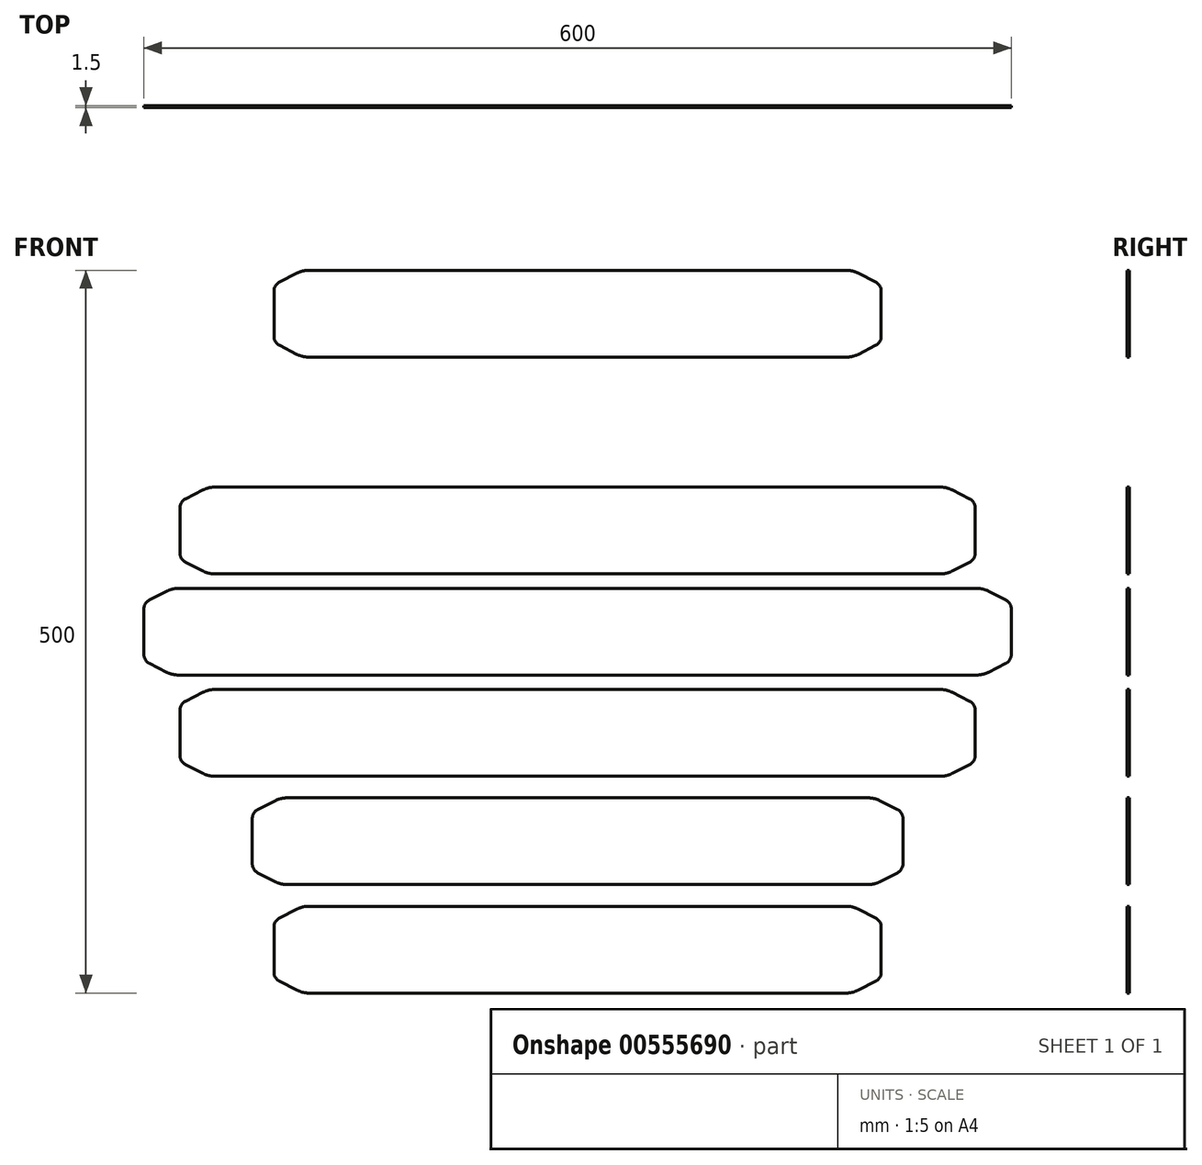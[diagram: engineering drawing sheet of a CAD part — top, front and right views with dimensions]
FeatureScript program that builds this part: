
annotation { "Feature Type Name" : "Feature", "Feature Type Description" : "" }
export const myFeature = defineFeature(function(context is Context, id is Id, definition is map)
    precondition{}
    {
        {
            var Q0;
            Q0=qCreatedBy(makeId("Front.planeOp"),FACE);
            var sketch = newSketch(context, id + "F0", { "sketchPlane" : qUnion([Q0])});
            skLineSegment(sketch, "E0", {"start": v(-284.17, 28.04) * mm, "end": v(-296.18, 21.92) * mm});
            skLineSegment(sketch, "E1", {"start": v(-300, 15.68) * mm, "end": v(-300, 0) * mm});
            skLineSegment(sketch, "E2", {"start": v(-300, 0) * mm, "end": v(0, 0) * mm, "construction": true});
            skLineSegment(sketch, "E3", {"start": v(-276, 30) * mm, "end": v(0, 30) * mm});
            skLineSegment(sketch, "E4", {"start": v(0, 30) * mm, "end": v(0, 0) * mm, "construction": true});
            skPoint(sketch, "E5.visualSharp", {"position": v(-280.32, 30) * mm});
            skArc(sketch, "E5.filletArc", {"start": v(-276, 30) * mm, "mid": v(-280.2, 29.5) * mm, "end": v(-284.17, 28.04) * mm});
            skPoint(sketch, "E6.visualSharp", {"position": v(-300, 19.97) * mm});
            skArc(sketch, "E6.filletArc", {"start": v(-296.18, 21.92) * mm, "mid": v(-298.97, 19.34) * mm, "end": v(-300, 15.68) * mm});
            skLineSegment(sketch, "E7.MirrorCS", {"start": v(-300, -15.68) * mm, "end": v(-300, 0) * mm});
            skArc(sketch, "E8.MirrorCS", {"start": v(-296.18, -21.92) * mm, "mid": v(-298.97, -19.34) * mm, "end": v(-300, -15.68) * mm});
            skLineSegment(sketch, "E9.MirrorCS", {"start": v(-284.17, -28.04) * mm, "end": v(-296.18, -21.92) * mm});
            skLineSegment(sketch, "E10.MirrorCS", {"start": v(-276, -30) * mm, "end": v(0, -30) * mm});
            skArc(sketch, "E11.MirrorCS", {"start": v(-276, -30) * mm, "mid": v(-280.2, -29.5) * mm, "end": v(-284.17, -28.04) * mm});
            skLineSegment(sketch, "E12.MirrorCS", {"start": v(276, 30) * mm, "end": v(0, 30) * mm});
            skLineSegment(sketch, "E13.MirrorCS", {"start": v(276, -30) * mm, "end": v(0, -30) * mm});
            skLineSegment(sketch, "E14.MirrorCS", {"start": v(300, -15.68) * mm, "end": v(300, 0) * mm});
            skLineSegment(sketch, "E15.MirrorCS", {"start": v(300, 15.68) * mm, "end": v(300, 0) * mm});
            skPoint(sketch, "E16.MirrorP", {"position": v(300, 19.97) * mm});
            skArc(sketch, "E17.MirrorCS", {"start": v(296.18, 21.92) * mm, "mid": v(298.97, 19.34) * mm, "end": v(300, 15.68) * mm});
            skLineSegment(sketch, "E18.MirrorCS", {"start": v(284.17, 28.04) * mm, "end": v(296.18, 21.92) * mm});
            skArc(sketch, "E19.MirrorCS", {"start": v(276, 30) * mm, "mid": v(280.2, 29.5) * mm, "end": v(284.17, 28.04) * mm});
            skArc(sketch, "E20.MirrorCS", {"start": v(276, -30) * mm, "mid": v(280.2, -29.5) * mm, "end": v(284.17, -28.04) * mm});
            skLineSegment(sketch, "E21.MirrorCS", {"start": v(284.17, -28.04) * mm, "end": v(296.18, -21.92) * mm});
            skArc(sketch, "E22.MirrorCS", {"start": v(296.18, -21.92) * mm, "mid": v(298.97, -19.34) * mm, "end": v(300, -15.68) * mm});
            skLineSegment(sketch, "E23", {"start": v(-259.17, -41.96) * mm, "end": v(-271.18, -48.08) * mm});
            skLineSegment(sketch, "E24", {"start": v(-275, -54.32) * mm, "end": v(-275, -70) * mm});
            skLineSegment(sketch, "E25", {"start": v(-275, -70) * mm, "end": v(0, -70) * mm, "construction": true});
            skLineSegment(sketch, "E26", {"start": v(-251, -40) * mm, "end": v(0, -40) * mm});
            skLineSegment(sketch, "E27", {"start": v(0, -40) * mm, "end": v(0, -70) * mm, "construction": true});
            skPoint(sketch, "E28.visualSharp", {"position": v(-255.32, -40) * mm});
            skArc(sketch, "E28.filletArc", {"start": v(-251, -40) * mm, "mid": v(-255.2, -40.5) * mm, "end": v(-259.17, -41.96) * mm});
            skPoint(sketch, "E29.visualSharp", {"position": v(-275, -50.03) * mm});
            skArc(sketch, "E29.filletArc", {"start": v(-271.18, -48.08) * mm, "mid": v(-273.97, -50.66) * mm, "end": v(-275, -54.32) * mm});
            skLineSegment(sketch, "E30.MirrorCS", {"start": v(-275, -85.68) * mm, "end": v(-275, -70) * mm});
            skArc(sketch, "E31.MirrorCS", {"start": v(-271.18, -91.92) * mm, "mid": v(-273.97, -89.34) * mm, "end": v(-275, -85.68) * mm});
            skLineSegment(sketch, "E32.MirrorCS", {"start": v(-259.17, -98.04) * mm, "end": v(-271.18, -91.92) * mm});
            skLineSegment(sketch, "E33.MirrorCS", {"start": v(-251, -100) * mm, "end": v(0, -100) * mm});
            skArc(sketch, "E34.MirrorCS", {"start": v(-251, -100) * mm, "mid": v(-255.2, -99.5) * mm, "end": v(-259.17, -98.04) * mm});
            skLineSegment(sketch, "E35.MirrorCS", {"start": v(251, -40) * mm, "end": v(0, -40) * mm});
            skLineSegment(sketch, "E36.MirrorCS", {"start": v(251, -100) * mm, "end": v(0, -100) * mm});
            skLineSegment(sketch, "E37.MirrorCS", {"start": v(275, -85.68) * mm, "end": v(275, -70) * mm});
            skLineSegment(sketch, "E38.MirrorCS", {"start": v(275, -54.32) * mm, "end": v(275, -70) * mm});
            skPoint(sketch, "E39.MirrorP", {"position": v(275, -50.03) * mm});
            skArc(sketch, "E40.MirrorCS", {"start": v(271.18, -48.08) * mm, "mid": v(273.97, -50.66) * mm, "end": v(275, -54.32) * mm});
            skLineSegment(sketch, "E41.MirrorCS", {"start": v(259.17, -41.96) * mm, "end": v(271.18, -48.08) * mm});
            skArc(sketch, "E42.MirrorCS", {"start": v(251, -40) * mm, "mid": v(255.2, -40.5) * mm, "end": v(259.17, -41.96) * mm});
            skArc(sketch, "E43.MirrorCS", {"start": v(251, -100) * mm, "mid": v(255.2, -99.5) * mm, "end": v(259.17, -98.04) * mm});
            skLineSegment(sketch, "E44.MirrorCS", {"start": v(259.17, -98.04) * mm, "end": v(271.18, -91.92) * mm});
            skArc(sketch, "E45.MirrorCS", {"start": v(271.18, -91.92) * mm, "mid": v(273.97, -89.34) * mm, "end": v(275, -85.68) * mm});
            skLineSegment(sketch, "E46", {"start": v(-209.17, -116.96) * mm, "end": v(-221.18, -123.08) * mm});
            skLineSegment(sketch, "E47", {"start": v(-225, -129.32) * mm, "end": v(-225, -145) * mm});
            skLineSegment(sketch, "E48", {"start": v(-225, -145) * mm, "end": v(0, -145) * mm, "construction": true});
            skLineSegment(sketch, "E49", {"start": v(-201, -115) * mm, "end": v(0, -115) * mm});
            skLineSegment(sketch, "E50", {"start": v(0, -115) * mm, "end": v(0, -145) * mm, "construction": true});
            skPoint(sketch, "E51.visualSharp", {"position": v(-205.32, -115) * mm});
            skArc(sketch, "E51.filletArc", {"start": v(-201, -115) * mm, "mid": v(-205.2, -115.5) * mm, "end": v(-209.17, -116.96) * mm});
            skPoint(sketch, "E52.visualSharp", {"position": v(-225, -125.03) * mm});
            skArc(sketch, "E52.filletArc", {"start": v(-221.18, -123.08) * mm, "mid": v(-223.97, -125.66) * mm, "end": v(-225, -129.32) * mm});
            skLineSegment(sketch, "E53.MirrorCS", {"start": v(-225, -160.68) * mm, "end": v(-225, -145) * mm});
            skArc(sketch, "E54.MirrorCS", {"start": v(-221.18, -166.92) * mm, "mid": v(-223.97, -164.34) * mm, "end": v(-225, -160.68) * mm});
            skLineSegment(sketch, "E55.MirrorCS", {"start": v(-209.17, -173.04) * mm, "end": v(-221.18, -166.92) * mm});
            skLineSegment(sketch, "E56.MirrorCS", {"start": v(-201, -175) * mm, "end": v(0, -175) * mm});
            skArc(sketch, "E57.MirrorCS", {"start": v(-201, -175) * mm, "mid": v(-205.2, -174.5) * mm, "end": v(-209.17, -173.04) * mm});
            skLineSegment(sketch, "E58.MirrorCS", {"start": v(201, -115) * mm, "end": v(0, -115) * mm});
            skLineSegment(sketch, "E59.MirrorCS", {"start": v(201, -175) * mm, "end": v(0, -175) * mm});
            skLineSegment(sketch, "E60.MirrorCS", {"start": v(225, -160.68) * mm, "end": v(225, -145) * mm});
            skLineSegment(sketch, "E61.MirrorCS", {"start": v(225, -129.32) * mm, "end": v(225, -145) * mm});
            skPoint(sketch, "E62.MirrorP", {"position": v(225, -125.03) * mm});
            skArc(sketch, "E63.MirrorCS", {"start": v(221.18, -123.08) * mm, "mid": v(223.97, -125.66) * mm, "end": v(225, -129.32) * mm});
            skLineSegment(sketch, "E64.MirrorCS", {"start": v(209.17, -116.96) * mm, "end": v(221.18, -123.08) * mm});
            skArc(sketch, "E65.MirrorCS", {"start": v(201, -115) * mm, "mid": v(205.2, -115.5) * mm, "end": v(209.17, -116.96) * mm});
            skArc(sketch, "E66.MirrorCS", {"start": v(201, -175) * mm, "mid": v(205.2, -174.5) * mm, "end": v(209.17, -173.04) * mm});
            skLineSegment(sketch, "E67.MirrorCS", {"start": v(209.17, -173.04) * mm, "end": v(221.18, -166.92) * mm});
            skArc(sketch, "E68.MirrorCS", {"start": v(221.18, -166.92) * mm, "mid": v(223.97, -164.34) * mm, "end": v(225, -160.68) * mm});
            skLineSegment(sketch, "E69", {"start": v(-194.17, -191.96) * mm, "end": v(-206.18, -198.08) * mm});
            skLineSegment(sketch, "E70", {"start": v(-210, -204.32) * mm, "end": v(-210, -220) * mm});
            skLineSegment(sketch, "E71", {"start": v(-210, -220) * mm, "end": v(0, -220) * mm, "construction": true});
            skLineSegment(sketch, "E72", {"start": v(-186, -190) * mm, "end": v(0, -190) * mm});
            skLineSegment(sketch, "E73", {"start": v(0, -190) * mm, "end": v(0, -220) * mm, "construction": true});
            skPoint(sketch, "E74.visualSharp", {"position": v(-190.32, -190) * mm});
            skArc(sketch, "E74.filletArc", {"start": v(-186, -190) * mm, "mid": v(-190.2, -190.5) * mm, "end": v(-194.17, -191.96) * mm});
            skPoint(sketch, "E75.visualSharp", {"position": v(-210, -200.03) * mm});
            skArc(sketch, "E75.filletArc", {"start": v(-206.18, -198.08) * mm, "mid": v(-208.97, -200.66) * mm, "end": v(-210, -204.32) * mm});
            skLineSegment(sketch, "E76.MirrorCS", {"start": v(-210, -235.68) * mm, "end": v(-210, -220) * mm});
            skArc(sketch, "E77.MirrorCS", {"start": v(-206.18, -241.92) * mm, "mid": v(-208.97, -239.34) * mm, "end": v(-210, -235.68) * mm});
            skLineSegment(sketch, "E78.MirrorCS", {"start": v(-194.17, -248.04) * mm, "end": v(-206.18, -241.92) * mm});
            skLineSegment(sketch, "E79.MirrorCS", {"start": v(-186, -250) * mm, "end": v(0, -250) * mm});
            skArc(sketch, "E80.MirrorCS", {"start": v(-186, -250) * mm, "mid": v(-190.2, -249.5) * mm, "end": v(-194.17, -248.04) * mm});
            skLineSegment(sketch, "E81.MirrorCS", {"start": v(186, -190) * mm, "end": v(0, -190) * mm});
            skLineSegment(sketch, "E82.MirrorCS", {"start": v(186, -250) * mm, "end": v(0, -250) * mm});
            skLineSegment(sketch, "E83.MirrorCS", {"start": v(210, -235.68) * mm, "end": v(210, -220) * mm});
            skLineSegment(sketch, "E84.MirrorCS", {"start": v(210, -204.32) * mm, "end": v(210, -220) * mm});
            skPoint(sketch, "E85.MirrorP", {"position": v(210, -200.03) * mm});
            skArc(sketch, "E86.MirrorCS", {"start": v(206.18, -198.08) * mm, "mid": v(208.97, -200.66) * mm, "end": v(210, -204.32) * mm});
            skLineSegment(sketch, "E87.MirrorCS", {"start": v(194.17, -191.96) * mm, "end": v(206.18, -198.08) * mm});
            skArc(sketch, "E88.MirrorCS", {"start": v(186, -190) * mm, "mid": v(190.2, -190.5) * mm, "end": v(194.17, -191.96) * mm});
            skArc(sketch, "E89.MirrorCS", {"start": v(186, -250) * mm, "mid": v(190.2, -249.5) * mm, "end": v(194.17, -248.04) * mm});
            skLineSegment(sketch, "E90.MirrorCS", {"start": v(194.17, -248.04) * mm, "end": v(206.18, -241.92) * mm});
            skArc(sketch, "E91.MirrorCS", {"start": v(206.18, -241.92) * mm, "mid": v(208.97, -239.34) * mm, "end": v(210, -235.68) * mm});
            skArc(sketch, "E92.MirrorCS", {"start": v(-221.18, 123.08) * mm, "mid": v(-223.97, 125.66) * mm, "end": v(-225, 129.32) * mm});
            skArc(sketch, "E93.MirrorCS", {"start": v(-271.18, 91.92) * mm, "mid": v(-273.97, 89.34) * mm, "end": v(-275, 85.68) * mm});
            skLineSegment(sketch, "E94.MirrorCS", {"start": v(-225, 129.32) * mm, "end": v(-225, 145) * mm});
            skLineSegment(sketch, "E95.MirrorCS", {"start": v(-259.17, 98.04) * mm, "end": v(-271.18, 91.92) * mm});
            skLineSegment(sketch, "E96.MirrorCS", {"start": v(-209.17, 116.96) * mm, "end": v(-221.18, 123.08) * mm});
            skLineSegment(sketch, "E97.MirrorCS", {"start": v(-210, 204.32) * mm, "end": v(-210, 220) * mm});
            skLineSegment(sketch, "E98.MirrorCS", {"start": v(-194.17, 191.96) * mm, "end": v(-206.18, 198.08) * mm});
            skArc(sketch, "E99.MirrorCS", {"start": v(206.18, 198.08) * mm, "mid": v(208.97, 200.66) * mm, "end": v(210, 204.32) * mm});
            skArc(sketch, "E100.MirrorCS", {"start": v(-251, 100) * mm, "mid": v(-255.2, 99.5) * mm, "end": v(-259.17, 98.04) * mm});
            skArc(sketch, "E101.MirrorCS", {"start": v(-201, 115) * mm, "mid": v(-205.2, 115.5) * mm, "end": v(-209.17, 116.96) * mm});
            skLineSegment(sketch, "E102.MirrorCS", {"start": v(210, 204.32) * mm, "end": v(210, 220) * mm});
            skArc(sketch, "E103.MirrorCS", {"start": v(-206.18, 198.08) * mm, "mid": v(-208.97, 200.66) * mm, "end": v(-210, 204.32) * mm});
            skArc(sketch, "E104.MirrorCS", {"start": v(-201, 175) * mm, "mid": v(-205.2, 174.5) * mm, "end": v(-209.17, 173.04) * mm});
            skArc(sketch, "E105.MirrorCS", {"start": v(-186, 250) * mm, "mid": v(-190.2, 249.5) * mm, "end": v(-194.17, 248.04) * mm});
            skLineSegment(sketch, "E106.MirrorCS", {"start": v(-275, 54.32) * mm, "end": v(-275, 70) * mm});
            skArc(sketch, "E107.MirrorCS", {"start": v(-186, 190) * mm, "mid": v(-190.2, 190.5) * mm, "end": v(-194.17, 191.96) * mm});
            skLineSegment(sketch, "E108.MirrorCS", {"start": v(-194.17, 248.04) * mm, "end": v(-206.18, 241.92) * mm});
            skLineSegment(sketch, "E109.MirrorCS", {"start": v(-209.17, 173.04) * mm, "end": v(-221.18, 166.92) * mm});
            skArc(sketch, "E110.MirrorCS", {"start": v(-251, 40) * mm, "mid": v(-255.2, 40.5) * mm, "end": v(-259.17, 41.96) * mm});
            skLineSegment(sketch, "E111.MirrorCS", {"start": v(209.17, 116.96) * mm, "end": v(221.18, 123.08) * mm});
            skLineSegment(sketch, "E112.MirrorCS", {"start": v(209.17, 173.04) * mm, "end": v(221.18, 166.92) * mm});
            skLineSegment(sketch, "E113.MirrorCS", {"start": v(-275, 85.68) * mm, "end": v(-275, 70) * mm});
            skArc(sketch, "E114.MirrorCS", {"start": v(201, 175) * mm, "mid": v(205.2, 174.5) * mm, "end": v(209.17, 173.04) * mm});
            skArc(sketch, "E115.MirrorCS", {"start": v(271.18, 48.08) * mm, "mid": v(273.97, 50.66) * mm, "end": v(275, 54.32) * mm});
            skLineSegment(sketch, "E116.MirrorCS", {"start": v(-259.17, 41.96) * mm, "end": v(-271.18, 48.08) * mm});
            skArc(sketch, "E117.MirrorCS", {"start": v(221.18, 123.08) * mm, "mid": v(223.97, 125.66) * mm, "end": v(225, 129.32) * mm});
            skLineSegment(sketch, "E118.MirrorCS", {"start": v(259.17, 41.96) * mm, "end": v(271.18, 48.08) * mm});
            skArc(sketch, "E119.MirrorCS", {"start": v(-271.18, 48.08) * mm, "mid": v(-273.97, 50.66) * mm, "end": v(-275, 54.32) * mm});
            skLineSegment(sketch, "E120.MirrorCS", {"start": v(-225, 160.68) * mm, "end": v(-225, 145) * mm});
            skLineSegment(sketch, "E121.MirrorCS", {"start": v(194.17, 191.96) * mm, "end": v(206.18, 198.08) * mm});
            skLineSegment(sketch, "E122.MirrorCS", {"start": v(-210, 235.68) * mm, "end": v(-210, 220) * mm});
            skArc(sketch, "E123.MirrorCS", {"start": v(251, 100) * mm, "mid": v(255.2, 99.5) * mm, "end": v(259.17, 98.04) * mm});
            skArc(sketch, "E124.MirrorCS", {"start": v(221.18, 166.92) * mm, "mid": v(223.97, 164.34) * mm, "end": v(225, 160.68) * mm});
            skArc(sketch, "E125.MirrorCS", {"start": v(251, 40) * mm, "mid": v(255.2, 40.5) * mm, "end": v(259.17, 41.96) * mm});
            skArc(sketch, "E126.MirrorCS", {"start": v(186, 190) * mm, "mid": v(190.2, 190.5) * mm, "end": v(194.17, 191.96) * mm});
            skArc(sketch, "E127.MirrorCS", {"start": v(206.18, 241.92) * mm, "mid": v(208.97, 239.34) * mm, "end": v(210, 235.68) * mm});
            skArc(sketch, "E128.MirrorCS", {"start": v(201, 115) * mm, "mid": v(205.2, 115.5) * mm, "end": v(209.17, 116.96) * mm});
            skArc(sketch, "E129.MirrorCS", {"start": v(186, 250) * mm, "mid": v(190.2, 249.5) * mm, "end": v(194.17, 248.04) * mm});
            skArc(sketch, "E130.MirrorCS", {"start": v(271.18, 91.92) * mm, "mid": v(273.97, 89.34) * mm, "end": v(275, 85.68) * mm});
            skLineSegment(sketch, "E131.MirrorCS", {"start": v(225, 129.32) * mm, "end": v(225, 145) * mm});
            skLineSegment(sketch, "E132.MirrorCS", {"start": v(0, 115) * mm, "end": v(0, 145) * mm, "construction": true});
            skLineSegment(sketch, "E133.MirrorCS", {"start": v(194.17, 248.04) * mm, "end": v(206.18, 241.92) * mm});
            skArc(sketch, "E134.MirrorCS", {"start": v(-221.18, 166.92) * mm, "mid": v(-223.97, 164.34) * mm, "end": v(-225, 160.68) * mm});
            skLineSegment(sketch, "E135.MirrorCS", {"start": v(275, 85.68) * mm, "end": v(275, 70) * mm});
            skLineSegment(sketch, "E136.MirrorCS", {"start": v(0, 190) * mm, "end": v(0, 220) * mm, "construction": true});
            skLineSegment(sketch, "E137.MirrorCS", {"start": v(210, 235.68) * mm, "end": v(210, 220) * mm});
            skArc(sketch, "E138.MirrorCS", {"start": v(-206.18, 241.92) * mm, "mid": v(-208.97, 239.34) * mm, "end": v(-210, 235.68) * mm});
            skLineSegment(sketch, "E139.MirrorCS", {"start": v(275, 54.32) * mm, "end": v(275, 70) * mm});
            skLineSegment(sketch, "E140.MirrorCS", {"start": v(0, 40) * mm, "end": v(0, 70) * mm, "construction": true});
            skLineSegment(sketch, "E141.MirrorCS", {"start": v(225, 160.68) * mm, "end": v(225, 145) * mm});
            skLineSegment(sketch, "E142.MirrorCS", {"start": v(259.17, 98.04) * mm, "end": v(271.18, 91.92) * mm});
            skLineSegment(sketch, "E143.MirrorCS", {"start": v(251, 40) * mm, "end": v(0, 40) * mm});
            skLineSegment(sketch, "E144.MirrorCS", {"start": v(-251, 40) * mm, "end": v(0, 40) * mm});
            skLineSegment(sketch, "E145.MirrorCS", {"start": v(201, 175) * mm, "end": v(0, 175) * mm});
            skPoint(sketch, "E146.MirrorP", {"position": v(-190.32, 190) * mm});
            skPoint(sketch, "E147.MirrorP", {"position": v(275, 50.03) * mm});
            skLineSegment(sketch, "E148.MirrorCS", {"start": v(-275, 70) * mm, "end": v(0, 70) * mm, "construction": true});
            skLineSegment(sketch, "E149.MirrorCS", {"start": v(201, 115) * mm, "end": v(0, 115) * mm});
            skPoint(sketch, "E150.MirrorP", {"position": v(-225, 125.03) * mm});
            skLineSegment(sketch, "E151.MirrorCS", {"start": v(-251, 100) * mm, "end": v(0, 100) * mm});
            skLineSegment(sketch, "E152.MirrorCS", {"start": v(-186, 250) * mm, "end": v(0, 250) * mm});
            skLineSegment(sketch, "E153.MirrorCS", {"start": v(-186, 190) * mm, "end": v(0, 190) * mm});
            skLineSegment(sketch, "E154.MirrorCS", {"start": v(-210, 220) * mm, "end": v(0, 220) * mm, "construction": true});
            skLineSegment(sketch, "E155.MirrorCS", {"start": v(-225, 145) * mm, "end": v(0, 145) * mm, "construction": true});
            skLineSegment(sketch, "E156.MirrorCS", {"start": v(186, 190) * mm, "end": v(0, 190) * mm});
            skLineSegment(sketch, "E157.MirrorCS", {"start": v(186, 250) * mm, "end": v(0, 250) * mm});
            skLineSegment(sketch, "E158.MirrorCS", {"start": v(-201, 115) * mm, "end": v(0, 115) * mm});
            skLineSegment(sketch, "E159.MirrorCS", {"start": v(-201, 175) * mm, "end": v(0, 175) * mm});
            skPoint(sketch, "E160.MirrorP", {"position": v(-255.32, 40) * mm});
            skPoint(sketch, "E161.MirrorP", {"position": v(-205.32, 115) * mm});
            skPoint(sketch, "E162.MirrorP", {"position": v(-210, 200.03) * mm});
            skPoint(sketch, "E163.MirrorP", {"position": v(225, 125.03) * mm});
            skLineSegment(sketch, "E164.MirrorCS", {"start": v(251, 100) * mm, "end": v(0, 100) * mm});
            skPoint(sketch, "E165.MirrorP", {"position": v(210, 200.03) * mm});
            skPoint(sketch, "E166.MirrorP", {"position": v(-275, 50.03) * mm});
            skSolve(sketch);
        }
        {
            var Q0;
            Q0=makeQuery(id+"F0.imprint","IMPRINT",FACE,{"disambiguationData":[TD([[makeQuery(id+"F0.imprint","IMPRINT",EDGE,{"derivedFrom":sQuery(id+"F0.wireOp",EDGE,"E0")}),1.0]])]});
            var Q1;
            Q1=makeQuery(id+"F0.imprint","IMPRINT",FACE,{"disambiguationData":[TD([[makeQuery(id+"F0.imprint","IMPRINT",EDGE,{"derivedFrom":sQuery(id+"F0.wireOp",EDGE,"E93.MirrorCS")}),1.0]])]});
            var Q2;
            Q2=makeQuery(id+"F0.imprint","IMPRINT",FACE,{"disambiguationData":[TD([[makeQuery(id+"F0.imprint","IMPRINT",EDGE,{"derivedFrom":sQuery(id+"F0.wireOp",EDGE,"E92.MirrorCS")}),-1.0]])]});
            var Q3;
            Q3=makeQuery(id+"F0.imprint","IMPRINT",FACE,{"disambiguationData":[TD([[makeQuery(id+"F0.imprint","IMPRINT",EDGE,{"derivedFrom":sQuery(id+"F0.wireOp",EDGE,"E23")}),1.0]])]});
            var Q4;
            Q4=makeQuery(id+"F0.imprint","IMPRINT",FACE,{"disambiguationData":[TD([[makeQuery(id+"F0.imprint","IMPRINT",EDGE,{"derivedFrom":sQuery(id+"F0.wireOp",EDGE,"E46")}),1.0]])]});
            var Q5;
            Q5=makeQuery(id+"F0.imprint","IMPRINT",FACE,{"disambiguationData":[TD([[makeQuery(id+"F0.imprint","IMPRINT",EDGE,{"derivedFrom":sQuery(id+"F0.wireOp",EDGE,"E69")}),1.0]])]});
            var Q6;
            Q6=makeQuery(id+"F0.imprint","IMPRINT",FACE,{"disambiguationData":[TD([[makeQuery(id+"F0.imprint","IMPRINT",EDGE,{"derivedFrom":sQuery(id+"F0.wireOp",EDGE,"E97.MirrorCS")}),-1.0]])]});
            extrude(context, id + "F1", {"entities" : qUnion([Q0, Q1, Q2, Q3, Q4, Q5, Q6]), "depth" : 1.5 * mm, "offsetDistance" : 25 * mm});
        }
    });
